# Revit family: Desk-Teknion-B_MSD_Secondary_High-R2018
name_source: partatom
category: Furniture
revit_build: Autodesk Revit 2018 (Build: 20170223_1515(x64)
units: mm (PartAtom-declared; Revit-internal decimal feet)

## family parameters
Always vertical = Yes
Cut with Voids When Loaded = No
OmniClass Number = 23.40.70.14.64.21
OmniClass Title = Systems Furniture
Room Calculation Point = No
Shared = Yes
Work Plane-Based = No

## types (6) — shared parameters
Assembly Code = E2020200
Manufacturer = Teknion
Manufacturer Fax = 416.661.4586
Part Number = B_MSD
Product Documentation Link = http://www.teknion.com
Product Line = Expansion Casegoods
Product Page URL = http://www.teknion.com
Sustainability Data = http://www.teknion.com
URL = http://www.teknion.com
Unit Weight URL = http://www.teknion.com
Warranty = http://www.teknion.com

## per-type parameters (varying)
| type | Description | Height | Model | Worksurface Thickness |
| 1 3/16" Worksurface Thickness, High Height | Secondary Desk - High, 1-3/16" Thick WS | 26.972 " | BMMSDH_____ | 1.189 " |
| 1" Worksurface Thickness, High Height | Secondary Desk - High, 1" Thick WS | 26.972 " | BDMSDH___ | 1.016 " |
| 1 9/16" Worksurface Thickness, High Height | Secondary Desk - High, 1-9/16" Thick WS | 26.972 " | BXMSDH_____ | 1.555 " |
| 1 3/16" Worksurface Thickness, Low Height | Secondary Desk - Low, 1-3/16" Thick WS | 17.425 " | BMMSDL_____ | 1.189 " |
| 1 9/16" Worksurface Thickness, Low Height | Secondary Desk - Low, 1-9/16" Thick WS | 17.425 " | BXMSDL_____ | 1.555 " |
| 1" Worksurface Thickness, Low Height | Secondary Desk - Low, 1" Thick WS | 17.425 " | BDMSDL___ | 1.016 " |

## geometry (parser evidence)
native form markers: Blend x2, Sweep x2
no freeform markers — native parametric forms only
